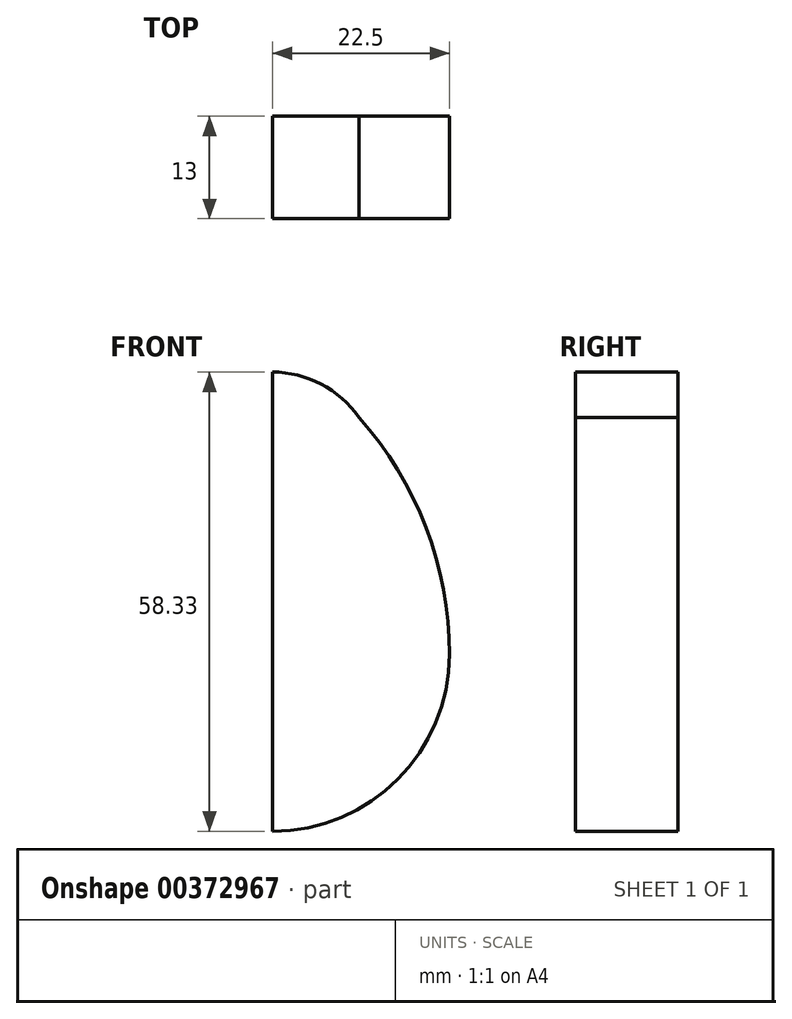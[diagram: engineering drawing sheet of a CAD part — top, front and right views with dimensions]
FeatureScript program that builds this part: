
annotation { "Feature Type Name" : "Feature", "Feature Type Description" : "" }
export const myFeature = defineFeature(function(context is Context, id is Id, definition is map)
    precondition{}
    {
        {
            var Q0;
            Q0=qCreatedBy(makeId("Front.planeOp"),FACE);
            var sketch = newSketch(context, id + "F0", { "sketchPlane" : qUnion([Q0])});
            skArc(sketch, "E0", {"start": v(0, -22.5) * mm, "mid": v(15.9, -15.9) * mm, "end": v(22.5, 0) * mm});
            skArc(sketch, "E1", {"start": v(22.5, 0) * mm, "mid": v(18.6, 18.33) * mm, "end": v(7.57, 33.48) * mm});
            skArc(sketch, "E2", {"start": v(10.98, 30.07) * mm, "mid": v(6.2, 34.3) * mm, "end": v(0, 35.83) * mm});
            skLineSegment(sketch, "E3", {"start": v(0, 35.83) * mm, "end": v(0, -22.5) * mm});
            skSolve(sketch);
        }
        {
            var Q0;
            Q0 = qSketchRegion(id + "F0", true);
            extrude(context, id + "F1", {"entities" : qUnion([Q0]), "depth" : 13 * mm});
        }
    });
